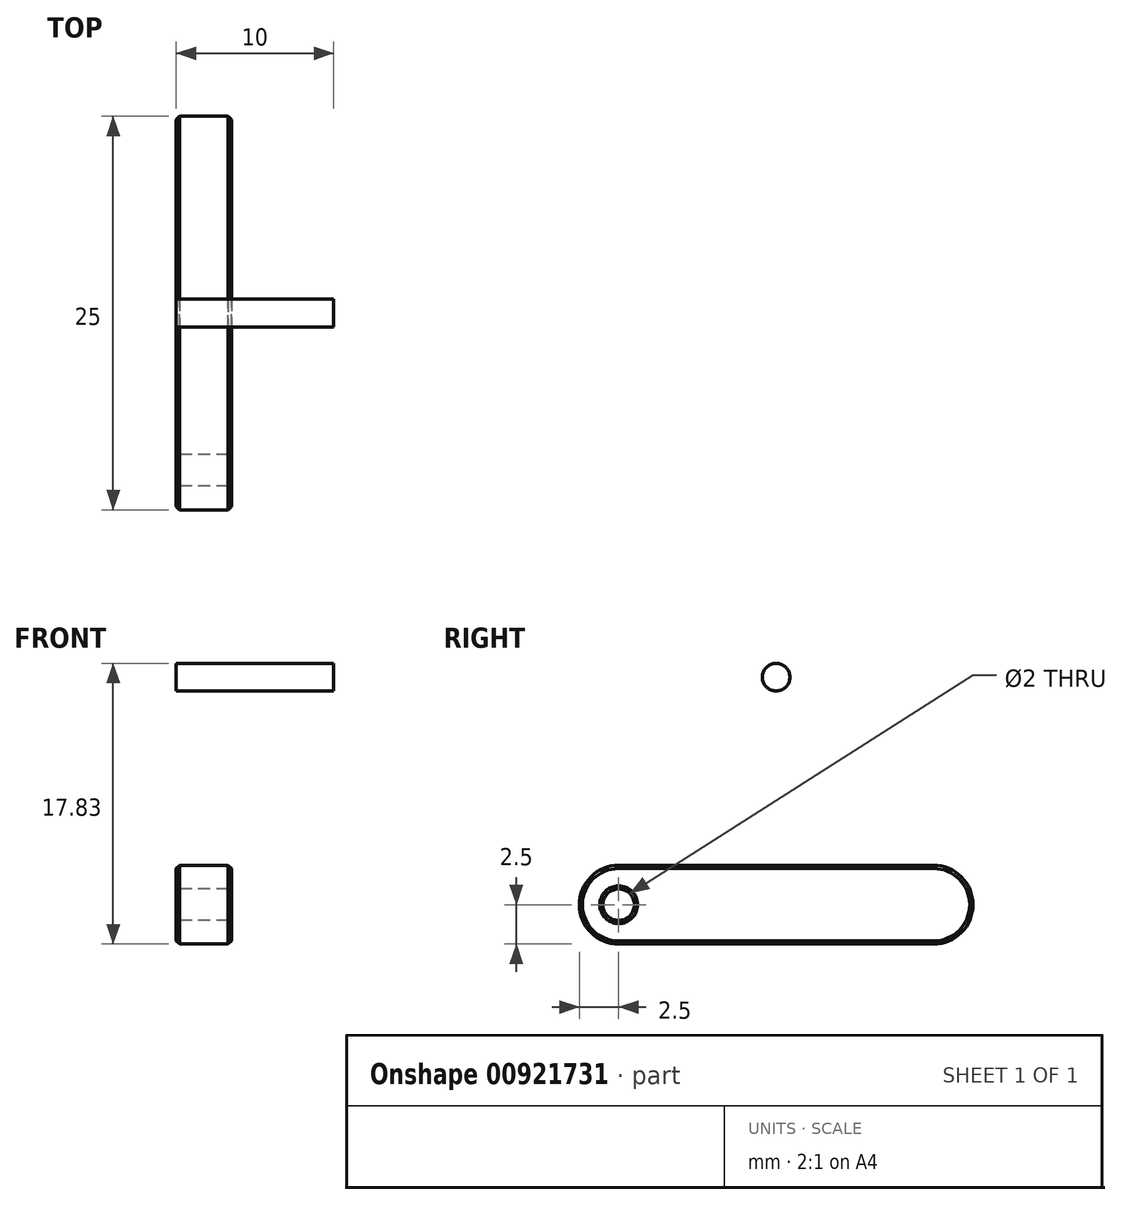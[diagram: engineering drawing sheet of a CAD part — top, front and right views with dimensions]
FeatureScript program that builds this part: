
annotation { "Feature Type Name" : "Feature", "Feature Type Description" : "" }
export const myFeature = defineFeature(function(context is Context, id is Id, definition is map)
    precondition{}
    {
        {
            var Q0;
            Q0=qCreatedBy(makeId("Right.planeOp"),FACE);
            var sketch = newSketch(context, id + "F0", { "sketchPlane" : qUnion([Q0])});
            skLineSegment(sketch, "E0.bottom", {"start": v(10, 2.5) * mm, "end": v(-10, 2.5) * mm});
            skLineSegment(sketch, "E0.top", {"start": v(10, -2.5) * mm, "end": v(-10, -2.5) * mm});
            skLineSegment(sketch, "E0.left", {"start": v(12.5, 0) * mm, "end": v(12.5, 0) * mm});
            skLineSegment(sketch, "E0.right", {"start": v(-12.5, 0) * mm, "end": v(-12.5, 0) * mm});
            skPoint(sketch, "E0.middle", {"position": v(0, 0) * mm});
            skLineSegment(sketch, "E1", {"start": v(-12.5, 0) * mm, "end": v(-10, 0) * mm});
            skCircle(sketch, "E2", {"center": v(-10, 0) * mm, "radius": 1 * mm});
            skPoint(sketch, "E3.visualSharp", {"position": v(-12.5, 2.5) * mm});
            skArc(sketch, "E3.filletArc", {"start": v(-10, 2.5) * mm, "mid": v(-11.77, 1.77) * mm, "end": v(-12.5, 0) * mm});
            skPoint(sketch, "E4.visualSharp", {"position": v(-12.5, -2.5) * mm});
            skArc(sketch, "E4.filletArc", {"start": v(-12.5, 0) * mm, "mid": v(-11.77, -1.77) * mm, "end": v(-10, -2.5) * mm});
            skPoint(sketch, "E5.visualSharp", {"position": v(12.5, 2.5) * mm});
            skArc(sketch, "E5.filletArc", {"start": v(12.5, 0) * mm, "mid": v(11.77, 1.77) * mm, "end": v(10, 2.5) * mm});
            skPoint(sketch, "E6.visualSharp", {"position": v(12.5, -2.5) * mm});
            skArc(sketch, "E6.filletArc", {"start": v(10, -2.5) * mm, "mid": v(11.77, -1.77) * mm, "end": v(12.5, 0) * mm});
            skCircle(sketch, "E7", {"center": v(0, 14.45) * mm, "radius": 0.87 * mm});
            skSolve(sketch);
        }
        {
            var Q0;
            Q0=makeQuery(id+"F0.imprint","IMPRINT",FACE,{"disambiguationData":[TD([[makeQuery(id+"F0.imprint","IMPRINT",EDGE,{"derivedFrom":sQuery(id+"F0.wireOp",EDGE,"E0.bottom")}),1.0]])]});
            extrude(context, id + "F1", {"entities" : qUnion([Q0]), "depth" : 3.5 * mm, "offsetDistance" : 25 * mm});
        }
        {
            var Q0;
            Q0=makeQuery(id+"F1.opExtrude","CAP_FACE",FACE,{"disambiguationData":[OSD([sQuery(id+"F0.wireOp",EDGE,"E0.bottom"),sQuery(id+"F0.wireOp",EDGE,"E0.top"),sQuery(id+"F0.wireOp",EDGE,"E2"),sQuery(id+"F0.wireOp",EDGE,"E3.filletArc"),sQuery(id+"F0.wireOp",EDGE,"E4.filletArc"),sQuery(id+"F0.wireOp",EDGE,"E5.filletArc"),sQuery(id+"F0.wireOp",EDGE,"E6.filletArc")])],"isStart":false});
            var Q1;
            Q1=makeQuery(id+"F1.opExtrude","CAP_FACE",FACE,{"disambiguationData":[OSD([sQuery(id+"F0.wireOp",EDGE,"E0.bottom"),sQuery(id+"F0.wireOp",EDGE,"E0.top"),sQuery(id+"F0.wireOp",EDGE,"E2"),sQuery(id+"F0.wireOp",EDGE,"E3.filletArc"),sQuery(id+"F0.wireOp",EDGE,"E4.filletArc"),sQuery(id+"F0.wireOp",EDGE,"E5.filletArc"),sQuery(id+"F0.wireOp",EDGE,"E6.filletArc")])],"isStart":true});
            chamfer(context, id + "F2", {"entities" : qUnion([Q0, Q1]), "width" : 0.2 * mm, "tangentPropagation" : true});
        }
        {
            var Q0;
            Q0=makeQuery(id+"F0.imprint","IMPRINT",FACE,{"disambiguationData":[TD([[makeQuery(id+"F0.imprint","IMPRINT",EDGE,{"derivedFrom":sQuery(id+"F0.wireOp",EDGE,"E7")}),1.0]])]});
            extrude(context, id + "F3", {"entities" : qUnion([Q0]), "depth" : 10 * mm, "offsetDistance" : 25 * mm});
        }
    });
